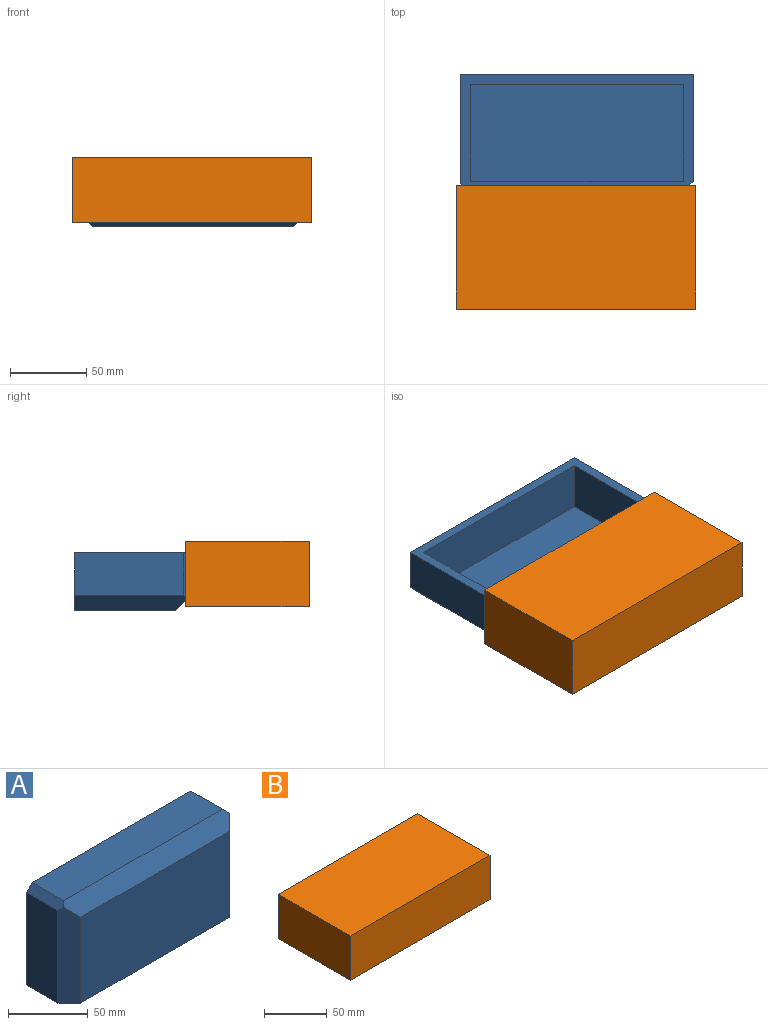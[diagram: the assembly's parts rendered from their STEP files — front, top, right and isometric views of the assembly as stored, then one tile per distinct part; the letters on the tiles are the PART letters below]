
ASSEMBLY  parts=2 mates=1
PART A: 16 faces, bbox 152.4x38.1x76.2 mm
  f0: plane 152.4x76.2mm, normal (0,1,0), area 2708mm2, adj f1,f2,f3,f4,f6,f7,f8,f9
  f1: plane 140.97x27.94mm, normal (0,0,1), area 3938.7mm2, adj f0,f11,f14,f15
  f2: plane 71.12x27.94mm, normal (-1,0,0), area 1987.1mm2, adj f0,f3,f12,f14
  f3: plane 152.4x38.1mm, normal (0,0,-1), area 5703.2mm2, adj f0,f2,f4,f5,f12,f13
  f4: plane 69.85x27.94mm, normal (1,0,0), area 1951.6mm2, adj f0,f3,f13,f15
  f5: plane 132.08x66.04mm, normal (0,-1,0), area 8722.6mm2, adj f3,f11,f12,f13
  f6: plane 139.7x33.02mm, normal (0,0,-1), area 4613mm2, adj f0,f7,f9,f10
  f7: plane 63.5x33.02mm, normal (-1,0,0), area 2096.9mm2, adj f0,f6,f8,f10
  f8: plane 139.7x33.02mm, normal (0,0,1), area 4613mm2, adj f0,f7,f9,f10
  f9: plane 63.5x33.02mm, normal (1,0,0), area 2096.9mm2, adj f0,f6,f8,f10
  f10: plane 139.7x63.5mm, normal (0,1,0), area 8871.8mm2, adj f6,f7,f8,f9
  f11: plane 146.69x10.16mm, normal (0,-0.71,0.71), area 2020.4mm2, adj f1,f5,f12,f13,f14,f15
  f12: plane 73.66x10.16mm, normal (-0.71,-0.71,0), area 1012.8mm2, adj f2,f3,f5,f11,f14
  f13: plane 73.03x10.16mm, normal (0.71,-0.71,0), area 1007.6mm2, adj f3,f4,f5,f11,f15
  f14: plane 30.48x5.08mm, normal (-0.71,0,0.71), area 209.9mm2, adj f0,f1,f2,f11,f12
  f15: plane 31.12x6.35mm, normal (0.71,0,0.71), area 265.2mm2, adj f0,f1,f4,f11,f13
PART B: 11 faces, bbox 157.5x81.3x43.2 mm
  f0: plane 157.48x43.18mm, normal (0,1,0), area 993.5mm2, adj f1,f3,f4,f5,f6,f7,f8,f9
  f1: plane 81.28x43.18mm, normal (-1,0,0), area 3509.7mm2, adj f0,f2,f4,f5
  f2: plane 157.48x43.18mm, normal (0,-1,0), area 6800mm2, adj f1,f3,f4,f5
  f3: plane 81.28x43.18mm, normal (1,0,0), area 3509.7mm2, adj f0,f2,f4,f5
  f4: plane 157.48x81.28mm, normal (0,0,1), area 12800mm2, adj f0,f1,f2,f3
  f5: plane 157.48x81.28mm, normal (0,0,-1), area 12800mm2, adj f0,f1,f2,f3
  f6: plane 152.4x76.2mm, normal (0,0,-1), area 11612.9mm2, adj f0,f7,f9,f10
  f7: plane 76.2x38.1mm, normal (-1,0,0), area 2903.2mm2, adj f0,f6,f8,f10
  f8: plane 152.4x76.2mm, normal (0,0,1), area 11612.9mm2, adj f0,f7,f9,f10
  f9: plane 76.2x38.1mm, normal (1,0,0), area 2903.2mm2, adj f0,f6,f8,f10
  f10: plane 152.4x38.1mm, normal (0,1,0), area 5806.4mm2, adj f6,f7,f8,f9
PLACE A rot(axis=(1,0,0),90deg) t=(-210.37,285.9,-32.78)mm
PLACE B t=(-193.71,208.24,-68.34)mm
MATE slider B.f10 <-> A.f1  axis (0,1,0) through (-181.01,160.85,-46.75)mm
